# Revit family: WRF-Welded Reduced Flange
name_source: partatom
category: Structural Framing
revit_build: Autodesk Revit Architecture 2012 (Build: 20110210_1515)
units: mm (PartAtom-declared; Revit-internal decimal feet)

## types (15) — shared parameters
Assembly Code = B10
bf_b = 1' - 9 5/8"
bf_t = 0' - 11 13/16"

## per-type parameters (varying)
| type | A | W | d | k | tf | tw |
| WRF71x365 | 0.74 SF | 365 | 5' - 10 7/8" | 0' - 0 3/4" | 0' - 1 3/4" | 0' - 0 11/16" |
| WRF71x323 | 0.66 SF | 323 | 5' - 10 7/8" | 0' - 0 3/4" | 0' - 1 3/8" | 0' - 0 11/16" |
| WRF71x280 | 0.57 SF | 280 | 5' - 10 7/8" | 0' - 0 3/4" | 0' - 1" | 0' - 0 11/16" |
| WRF63x330 | 0.67 SF | 330 | 5' - 3" | 0' - 0 11/16" | 0' - 1 3/4" | 0' - 0 5/8" |
| WRF63x287 | 0.59 SF | 287 | 5' - 3" | 0' - 0 11/16" | 0' - 1 3/8" | 0' - 0 5/8" |
| WRF63x243 | 0.5 SF | 243 | 5' - 3" | 0' - 0 11/16" | 0' - 1" | 0' - 0 5/8" |
| WRF55x278 | 0.57 SF | 278 | 4' - 7 1/8" | 0' - 0 5/8" | 0' - 1 9/16" | 0' - 0 9/16" |
| WRF55x234 | 0.48 SF | 234 | 4' - 7 1/8" | 0' - 0 5/8" | 0' - 1 3/16" | 0' - 0 9/16" |
| WRF55x191 | 0.39 SF | 191 | 4' - 7 1/8" | 0' - 0 5/8" | 0' - 0 13/16" | 0' - 0 9/16" |
| WRF47x251 | 0.51 SF | 251 | 3' - 11 1/4" | 0' - 0 9/16" | 0' - 1 9/16" | 0' - 0 1/2" |
| WRF47x208 | 0.42 SF | 208 | 3' - 11 1/4" | 0' - 0 9/16" | 0' - 1 3/16" | 0' - 0 1/2" |
| WRF47x164 | 0.33 SF | 164 | 3' - 11 1/4" | 0' - 0 9/16" | 0' - 0 13/16" | 0' - 0 1/2" |
| WRF39x228 | 0.47 SF | 228 | 3' - 3 3/8" | 0' - 0 9/16" | 0' - 1 9/16" | 0' - 0 3/8" |
| WRF39x185 | 0.38 SF | 185 | 3' - 3 3/8" | 0' - 0 9/16" | 0' - 1 3/16" | 0' - 0 3/8" |
| WRF39x141 | 0.29 SF | 141 | 3' - 3 3/8" | 0' - 0 9/16" | 0' - 0 13/16" | 0' - 0 3/8" |

## geometry (parser evidence)
native form markers: Sweep x2
no freeform markers — native parametric forms only
